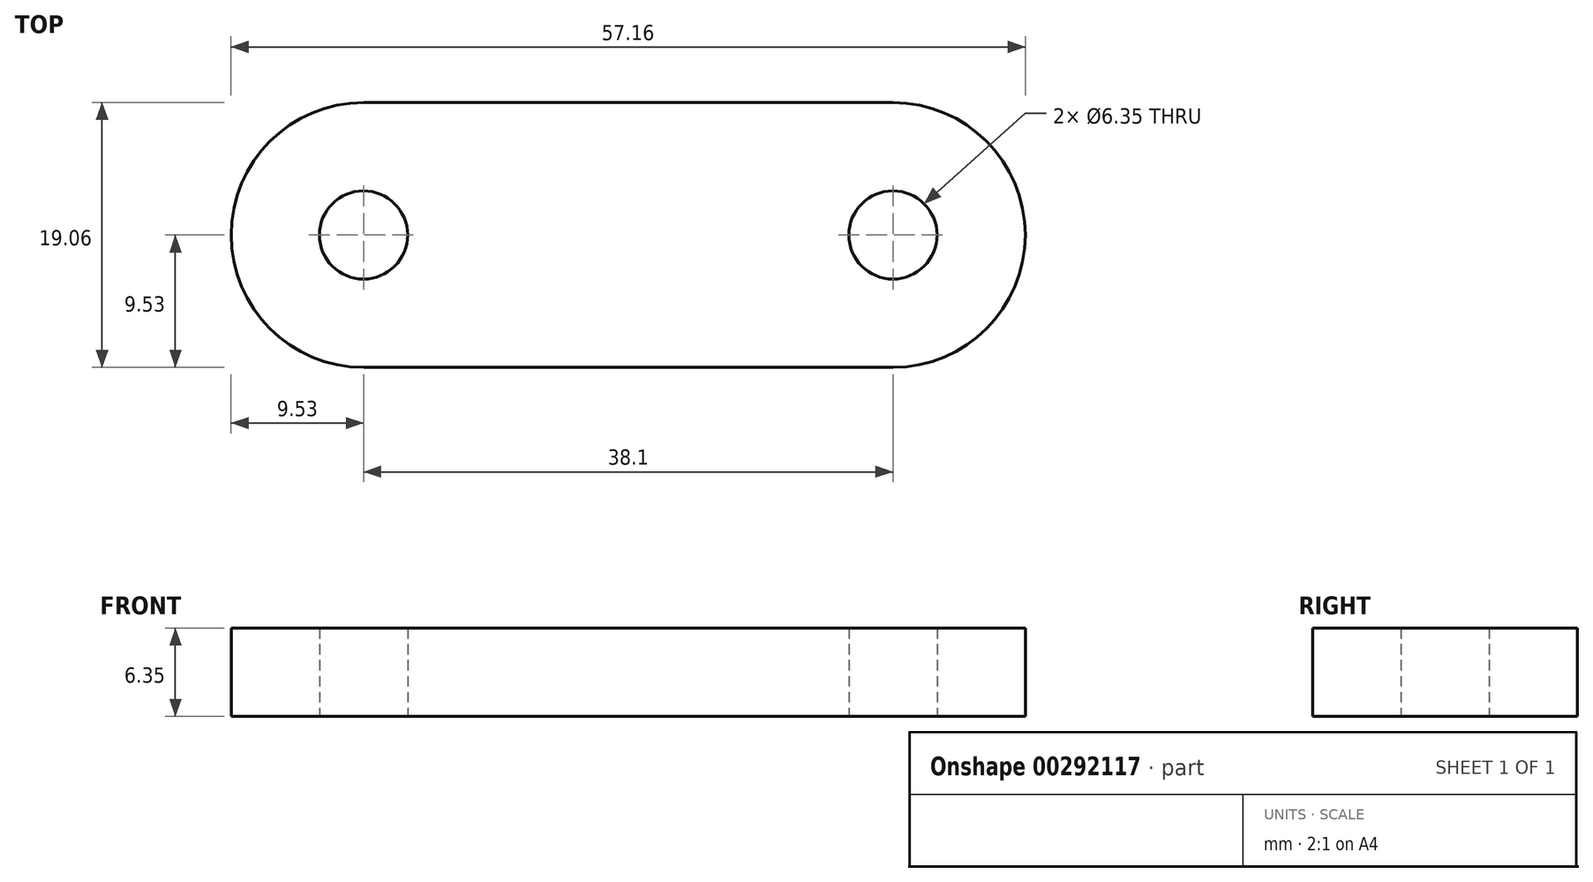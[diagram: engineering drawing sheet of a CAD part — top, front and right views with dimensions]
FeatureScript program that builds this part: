
annotation { "Feature Type Name" : "Feature", "Feature Type Description" : "" }
export const myFeature = defineFeature(function(context is Context, id is Id, definition is map)
    precondition{}
    {
        {
            var Q0;
            Q0=qCreatedBy(makeId("Top.planeOp"),FACE);
            var sketch = newSketch(context, id + "F0", { "sketchPlane" : qUnion([Q0])});
            skLineSegment(sketch, "E0.bottom", {"start": v(19.05, 9.53) * mm, "end": v(-19.05, 9.53) * mm});
            skLineSegment(sketch, "E0.top", {"start": v(19.05, -9.53) * mm, "end": v(-19.05, -9.53) * mm});
            skLineSegment(sketch, "E0.left", {"start": v(19.05, 9.53) * mm, "end": v(19.05, -9.53) * mm});
            skLineSegment(sketch, "E0.right", {"start": v(-19.05, 9.53) * mm, "end": v(-19.05, -9.53) * mm});
            skPoint(sketch, "E0.middle", {"position": v(0, 0) * mm});
            skArc(sketch, "E1", {"start": v(-19.05, 9.53) * mm, "mid": v(-28.58, 0) * mm, "end": v(-19.05, -9.53) * mm});
            skArc(sketch, "E2", {"start": v(19.05, -9.53) * mm, "mid": v(28.58, 0) * mm, "end": v(19.05, 9.53) * mm});
            skCircle(sketch, "E3", {"center": v(-19.05, 0) * mm, "radius": 3.18 * mm});
            skCircle(sketch, "E4", {"center": v(19.05, 0) * mm, "radius": 3.18 * mm});
            skSolve(sketch);
        }
        {
            var Q0;
            Q0 = qSketchRegion(id + "F0", true);
            extrude(context, id + "F1", {"entities" : qUnion([Q0]), "depth" : 6.35 * mm});
        }
    });
